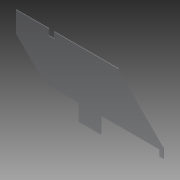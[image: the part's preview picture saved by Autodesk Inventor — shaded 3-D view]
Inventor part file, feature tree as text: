
AUTODESK INVENTOR PART (.ipt)
format: ipt  version: 2014 (Build 180170000, 170)  size: 340,992 bytes
history: native  units: in
note: dims shown in document units (in); Inventor stores cm internally (conversion verified against a paired STEP export)
features: reference x14, extrude x6, sketch x6, projected_geometry x1
ambient origin geometry x8: Origin, YZ Plane, XZ Plane, XY Plane, X Axis, Y Axis, Z Axis, Center Point
bodies: Solid1 (feature_tree)
feature tree (27):
  extrude  "Extrusion1"  Depth=10.125in
  extrude  "Extrusion2"  Depth=1.125in
  extrude  "Extrusion4"  Depth=0.75in
  extrude  "Extrusion5"  Depth=1.0in
  extrude  "Extrusion6"  Depth=6.0in
  extrude  "Extrusion7"  Depth=3.0in
  sketch  "Sketch1"  dims[d0=27.0in d1=10.125in]
  sketch  "Sketch2"  dims[d2=0.75in d3=1.125in]
  reference  "Reference1"
  reference  "Reference2"
  reference  "Reference3"
  reference  "Reference4"
  reference  "Reference5"
  reference  "Reference6"
  reference  "Reference7"
  reference  "Reference8"
  reference  "Reference9"
  reference  "Reference10"
  sketch  "Sketch3"  dims[d4=1.125in d5=0.75in]
  projected_geometry  "Projected Loop1"
  reference  "Reference11"
  sketch  "Sketch4"  dims[d6=1.125in d7=1.0in]
  sketch  "Sketch5"  dims[d8=6.0in d9=6.0in]
  reference  "Reference12"
  sketch  "Sketch6"  dims[d10=0.125in d11=0.0in d12=3.0in d13=4.0in d14=11.5in d15=1.0in d16=0.0in d17=1.0in d18=0.25in d19=1.0in d20=2.0in d21=0.25in d22=0.25in d23=1.0in d24=1.0in d25=0.25in d26=0.25in d27=2.0in d31=3.0in d33=0.125in d34=0.125in d35=0.125in d36=1.0in d37=0.0in d38=1.25in d39=1.25in d40=2.0in d41=1.0in d42=2.0in d43=1.25in d44=4.75in d45=1.0in d46=0.0in d47=0.163in d48=2.3622in d50=1.0in d51=0.3937in d53=1.0in d55=1.0in d56=0.0in d57=0.163in d58=0.163in d59=1.9685in d61=1.0in d62=0.3937in d64=1.0in d66=1.9685in d68=1.0in d69=0.3937in d71=1.0in d73=1.0in d74=0.0in d76=0.25in d77=1.0in]
  reference  "Reference13"
  reference  "Reference14"
